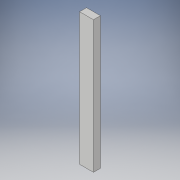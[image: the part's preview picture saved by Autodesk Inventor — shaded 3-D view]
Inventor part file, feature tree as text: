
AUTODESK INVENTOR PART (.ipt)
format: ipt  version: 2018 (Build 220112000, 112)  size: 92,160 bytes
history: native  units: in
note: dims shown in document units (in); Inventor stores cm internally (conversion verified against a paired STEP export)
features: extrude x1, sketch x1
ambient origin geometry x8: Origin, YZ Plane, XZ Plane, XY Plane, X Axis, Y Axis, Z Axis, Center Point
bodies: Solid1 (feature_tree)
feature tree (2):
  extrude  "Extrusion1"  Depth=19.0in
  sketch  "Sketch1"  dims[d0=2.0in d1=19.0in d2=1.0in d3=0.0in]
